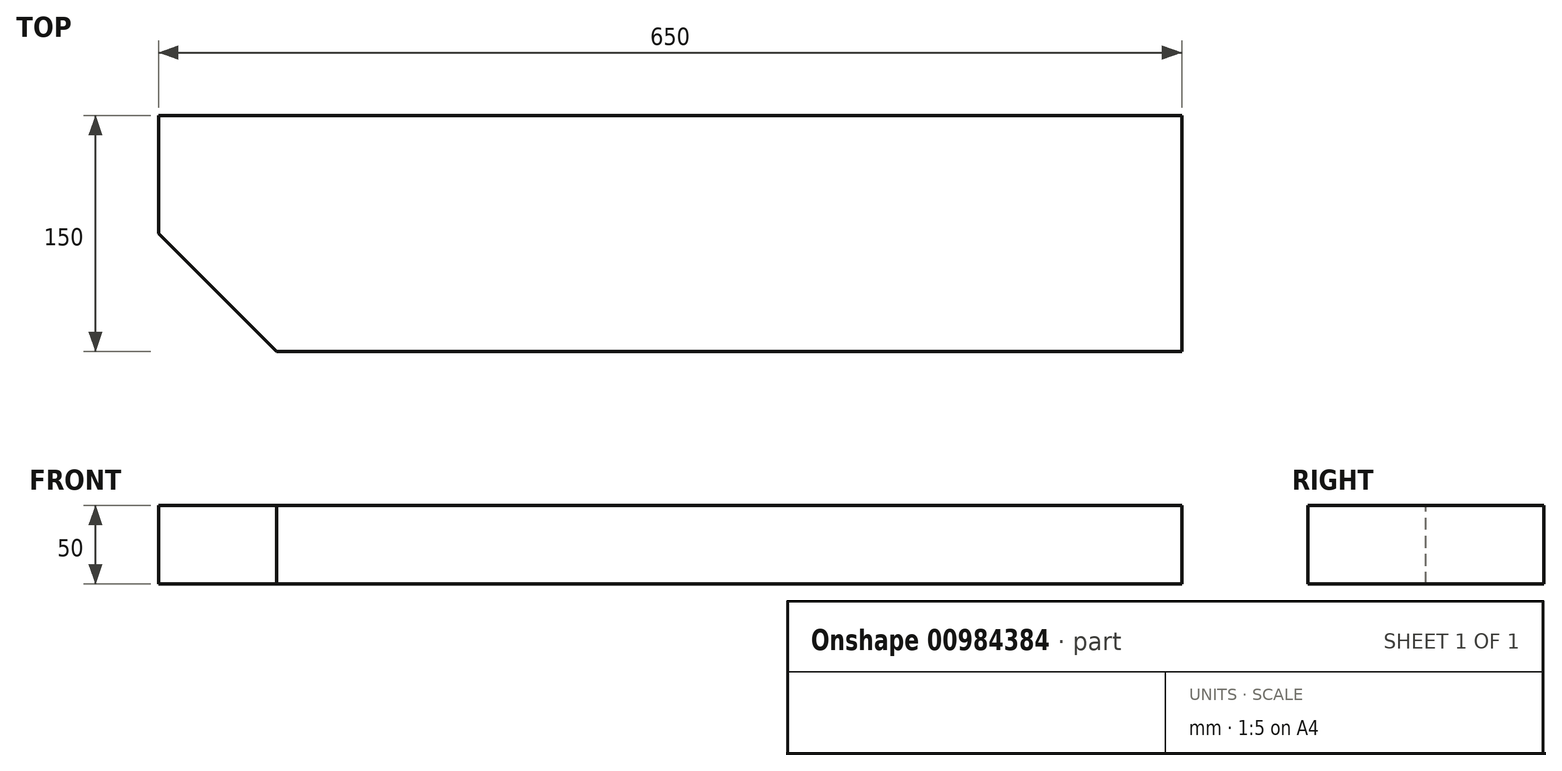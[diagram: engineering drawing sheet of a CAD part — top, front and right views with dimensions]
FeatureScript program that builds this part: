
annotation { "Feature Type Name" : "Feature", "Feature Type Description" : "" }
export const myFeature = defineFeature(function(context is Context, id is Id, definition is map)
    precondition{}
    {
        {
            var Q0;
            Q0=qCreatedBy(makeId("Right.planeOp"),FACE);
            var sketch = newSketch(context, id + "F0", { "sketchPlane" : qUnion([Q0])});
            skLineSegment(sketch, "E0.bottom", {"start": v(75, 25) * mm, "end": v(-75, 25) * mm});
            skLineSegment(sketch, "E0.top", {"start": v(75, -25) * mm, "end": v(-75, -25) * mm});
            skLineSegment(sketch, "E0.left", {"start": v(75, 25) * mm, "end": v(75, -25) * mm});
            skLineSegment(sketch, "E0.right", {"start": v(-75, 25) * mm, "end": v(-75, -25) * mm});
            skPoint(sketch, "E0.middle", {"position": v(0, 0) * mm});
            skSolve(sketch);
        }
        {
            var Q0;
            Q0=makeQuery(id+"F0.imprint","IMPRINT",FACE,{"disambiguationData":[TD([[makeQuery(id+"F0.imprint","IMPRINT",EDGE,{"derivedFrom":sQuery(id+"F0.wireOp",EDGE,"E0.bottom")}),1.0]])]});
            extrude(context, id + "F1", {"entities" : qUnion([Q0]), "endBound" : BoundingType.SYMMETRIC, "depth" : 650 * mm, "offsetDistance" : 25 * mm});
        }
        {
            var Q0;
            Q0=makeQuery(id+"F1.opExtrude","SWEPT_FACE",FACE,{"disambiguationData":[OSD([sQuery(id+"F0.wireOp",EDGE,"E0.bottom")])]});
            var sketch = newSketch(context, id + "F2", { "sketchPlane" : qUnion([Q0])});
            skLineSegment(sketch, "E1", {"start": v(-325, 0) * mm, "end": v(-250, -75) * mm});
            skLineSegment(sketch, "E2", {"start": v(-250, -75) * mm, "end": v(-325, -75) * mm});
            skLineSegment(sketch, "E3", {"start": v(-325, -75) * mm, "end": v(-325, 0) * mm});
            skSolve(sketch);
        }
        {
            var Q0;
            Q0 = qSketchRegion(id + "F2", true);
            extrude(context, id + "F3", {"entities" : qUnion([Q0]), "operationType" : NewBodyOperationType.REMOVE, "endBound" : BoundingType.THROUGH_ALL, "oppositeDirection" : true, "depth" : 25 * mm, "offsetDistance" : 25 * mm});
        }
    });
